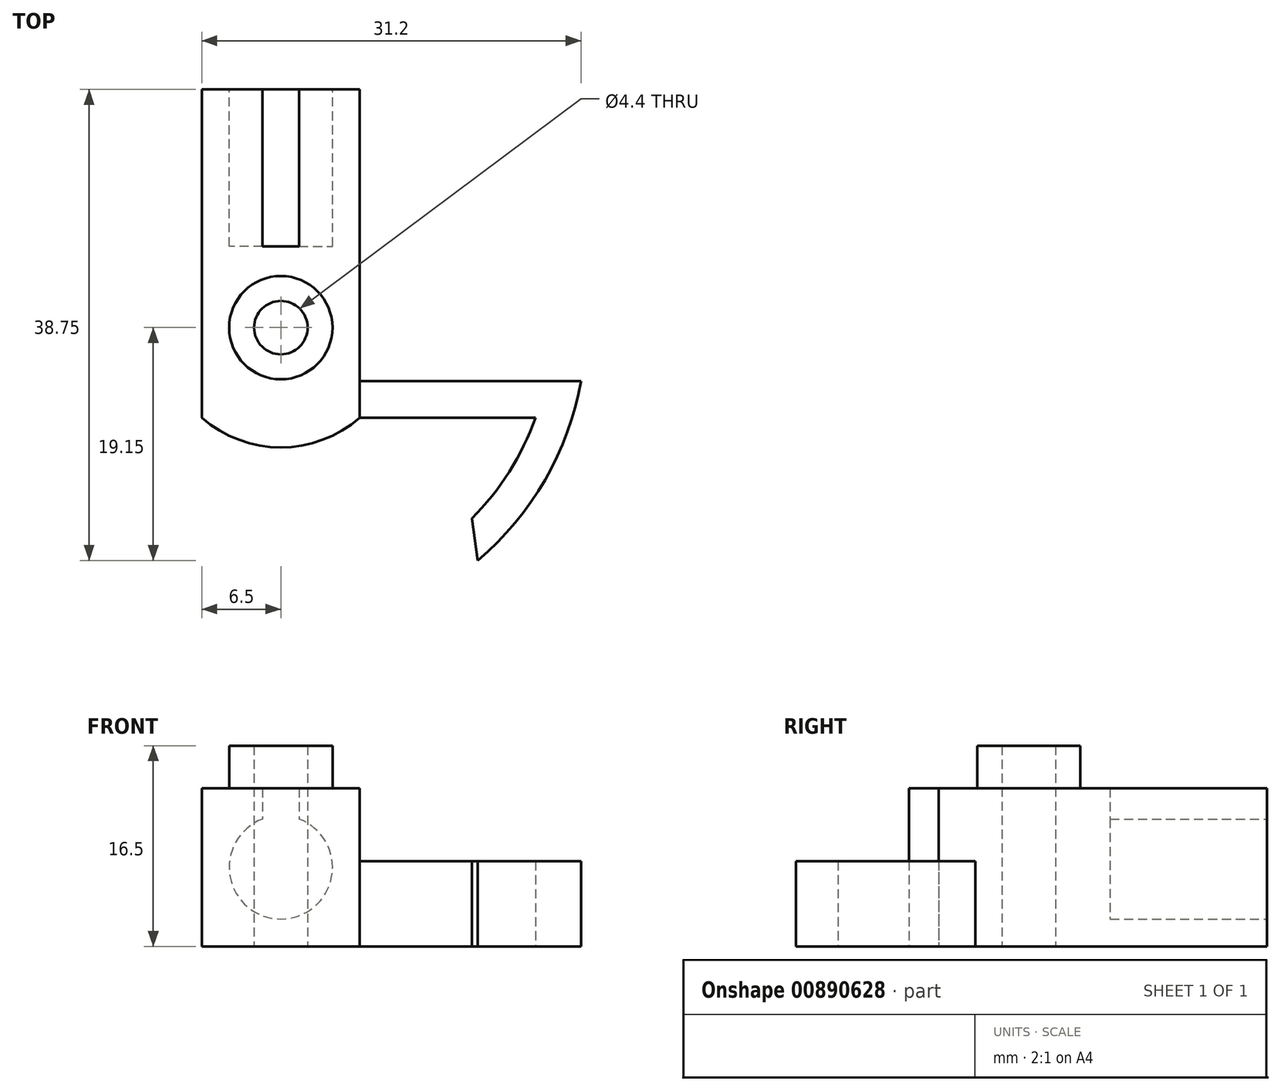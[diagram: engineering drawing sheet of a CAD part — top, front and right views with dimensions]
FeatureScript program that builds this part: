
annotation { "Feature Type Name" : "Feature", "Feature Type Description" : "" }
export const myFeature = defineFeature(function(context is Context, id is Id, definition is map)
    precondition{}
    {
        {
            var Q0;
            Q0=qCreatedBy(makeId("Top.planeOp"),FACE);
            var sketch = newSketch(context, id + "F0", { "sketchPlane" : qUnion([Q0])});
            skCircle(sketch, "E0", {"center": v(0, 0) * mm, "radius": 22.22 * mm, "construction": true});
            skLineSegment(sketch, "E1", {"start": v(0, 0) * mm, "end": v(-15.71, -15.71) * mm, "construction": true});
            skLineSegment(sketch, "E2", {"start": v(0, 0) * mm, "end": v(15.71, -15.71) * mm, "construction": true});
            skLineSegment(sketch, "E3", {"start": v(-6.5, -4.4) * mm, "end": v(6.5, -4.4) * mm});
            skLineSegment(sketch, "E4", {"start": v(-20.95, -7.4) * mm, "end": v(20.95, -7.4) * mm, "construction": true});
            skLineSegment(sketch, "E5", {"start": v(-15.71, -15.71) * mm, "end": v(15.71, -15.71) * mm, "construction": true});
            skArc(sketch, "E6", {"start": v(-11.71, -15.71) * mm, "mid": v(-15.5, -12) * mm, "end": v(-18.15, -7.4) * mm});
            skArc(sketch, "E7", {"start": v(15.71, -15.71) * mm, "mid": v(18.8, -11.85) * mm, "end": v(20.95, -7.4) * mm});
            skLineSegment(sketch, "E8", {"start": v(15.71, -15.71) * mm, "end": v(16.21, -19.15) * mm});
            skArc(sketch, "E9", {"start": v(16.21, -19.15) * mm, "mid": v(21.75, -12.52) * mm, "end": v(24.7, -4.4) * mm});
            skLineSegment(sketch, "E10", {"start": v(-18.15, -7.4) * mm, "end": v(20.95, -7.4) * mm});
            skLineSegment(sketch, "E11", {"start": v(-15.71, -15.71) * mm, "end": v(-11.71, -15.71) * mm});
            skLineSegment(sketch, "E12", {"start": v(20.95, -7.4) * mm, "end": v(23.95, -7.4) * mm, "construction": true});
            skLineSegment(sketch, "E13", {"start": v(-6.5, 19.6) * mm, "end": v(-6.5, -4.4) * mm});
            skLineSegment(sketch, "E14", {"start": v(-6.5, 19.6) * mm, "end": v(6.5, 19.6) * mm});
            skLineSegment(sketch, "E15", {"start": v(6.5, 19.6) * mm, "end": v(6.5, -4.4) * mm});
            skLineSegment(sketch, "E16", {"start": v(-6.5, -4.4) * mm, "end": v(-6.5, -7.4) * mm});
            skLineSegment(sketch, "E17", {"start": v(6.5, -4.4) * mm, "end": v(6.5, -7.4) * mm});
            skArc(sketch, "E18", {"start": v(-6.5, -7.4) * mm, "mid": v(0, -9.85) * mm, "end": v(6.5, -7.4) * mm});
            skLineSegment(sketch, "E19", {"start": v(6.5, -4.4) * mm, "end": v(24.7, -4.4) * mm});
            skLineSegment(sketch, "E20", {"start": v(-6.5, -4.4) * mm, "end": v(-21.78, -4.4) * mm});
            skArc(sketch, "E21", {"start": v(-21.78, -4.4) * mm, "mid": v(-19.58, -10.5) * mm, "end": v(-15.71, -15.71) * mm});
            skSolve(sketch);
        }
        {
            var Q0;
            Q0=qCreatedBy(makeId("Top.planeOp"),FACE);
            var sketch = newSketch(context, id + "F1", { "sketchPlane" : qUnion([Q0])});
            skCircle(sketch, "E22", {"center": v(0, 0) * mm, "radius": 2.2 * mm});
            skCircle(sketch, "E23", {"center": v(0, 0) * mm, "radius": 4.25 * mm});
            skSolve(sketch);
        }
        {
            var Q0;
            Q0=makeQuery(id+"F0.imprint","IMPRINT",FACE,{"disambiguationData":[TD([[makeQuery(id+"F0.imprint","IMPRINT",EDGE,{"derivedFrom":sQuery(id+"F0.wireOp",EDGE,"E3")}),1.0]])]});
            var Q1;
            Q1=makeQuery(id+"F0.imprint","IMPRINT",FACE,{"disambiguationData":[TD([[makeQuery(id+"F0.imprint","IMPRINT",EDGE,{"derivedFrom":sQuery(id+"F0.wireOp",EDGE,"E3")}),-1.0]])]});
            var Q2;
            {var subQ0=sQuery(id+"F0.wireOp",EDGE,"E18");Q2=makeQuery(id+"F0.imprint","IMPRINT",FACE,{"disambiguationData":[TD([[makeQuery(id+"F0.imprint","IMPRINT",EDGE,{"derivedFrom":subQ0}),1.0]])]});}
            extrude(context, id + "F2", {"entities" : qUnion([Q0, Q1, Q2]), "depth" : 13 * mm, "offsetDistance" : 25 * mm});
        }
        {
            var Q0;
            Q0=makeQuery(id+"F1.imprint","IMPRINT",FACE,{"disambiguationData":[TD([[makeQuery(id+"F1.imprint","IMPRINT",EDGE,{"derivedFrom":sQuery(id+"F1.wireOp",EDGE,"E22")}),1.0]])]});
            var Q1;
            Q1=makeQuery(id+"F2.opExtrude","CAP_FACE",FACE,{"disambiguationData":[OSD([sQuery(id+"F0.wireOp",EDGE,"E3"),sQuery(id+"F0.wireOp",EDGE,"KbbF9yi9-xrPk-JePT-w6c5-kPLa8MpGTuoP"),sQuery(id+"F0.wireOp",EDGE,"eadea0ab-e075-4038-b9cd-73dca94fccad"),sQuery(id+"F0.wireOp",EDGE,"E6"),sQuery(id+"F0.wireOp",EDGE,"E7"),sQuery(id+"F0.wireOp",EDGE,"E8"),sQuery(id+"F0.wireOp",EDGE,"E9"),sQuery(id+"F0.wireOp",EDGE,"E10"),sQuery(id+"F0.wireOp",EDGE,"hkPcLw81-8III-o7XO-lbjo-IzFt7Bc78l21"),sQuery(id+"F0.wireOp",EDGE,"Xk3sj3rP-0Nv0-YBO2-xSXg-Fs2LWpVnRU2r"),sQuery(id+"F0.wireOp",EDGE,"E11"),sQuery(id+"F0.wireOp",EDGE,"c4789ed1-a124-472e-85bf-6a12fd7359ae"),sQuery(id+"F0.wireOp",EDGE,"4b91fc80-4ab7-43a4-bafb-29e8abb85020"),sQuery(id+"F0.wireOp",EDGE,"E13"),sQuery(id+"F0.wireOp",EDGE,"E14"),sQuery(id+"F0.wireOp",EDGE,"E15"),sQuery(id+"F0.wireOp",EDGE,"E18")])],"isStart":false});
            extrude(context, id + "F3", {"entities" : qUnion([Q0]), "operationType" : NewBodyOperationType.REMOVE, "endBound" : BoundingType.UP_TO_SURFACE, "depth" : 25 * mm, "endBoundEntityFace" : qUnion([Q1]), "offsetDistance" : 25 * mm});
        }
        {
            var Q0;
            Q0=makeQuery(id+"F2.opExtrude","SWEPT_FACE",FACE,{"disambiguationData":[OSD([sQuery(id+"F0.wireOp",EDGE,"E14")])]});
            var sketch = newSketch(context, id + "F4", { "sketchPlane" : qUnion([Q0])});
            skLineSegment(sketch, "E24", {"start": v(-6.5, 6.5) * mm, "end": v(0, 6.5) * mm, "construction": true});
            skCircle(sketch, "E25", {"center": v(0, 6.5) * mm, "radius": 4.25 * mm});
            skLineSegment(sketch, "E26", {"start": v(-1.5, 13) * mm, "end": v(-1.5, 10.48) * mm});
            skLineSegment(sketch, "E27", {"start": v(1.5, 13) * mm, "end": v(1.5, 10.48) * mm});
            skSolve(sketch);
        }
        {
            var Q0;
            {var subQ0=sQuery(id+"F4.wireOp",EDGE,"E25");var subQ1=makeQuery(id+"F4.imprint","INTERSECT",VERTEX,{"derivedFrom":[subQ0,sQuery(id+"F4.wireOp",EDGE,"E26")]});Q0=makeQuery(id+"F4.imprint","IMPRINT",FACE,{"disambiguationData":[TD([[makeQuery(id+"F4.imprint","IMPRINT",EDGE,{"disambiguationData":[TD([[subQ1,1.0]])],"derivedFrom":subQ0}),1.0]])]});}
            var Q1;
            {var subQ0=sQuery(id+"F4.wireOp",EDGE,"E26");Q1=makeQuery(id+"F4.imprint","IMPRINT",FACE,{"disambiguationData":[TD([[makeQuery(id+"F4.imprint","IMPRINT",EDGE,{"derivedFrom":subQ0}),1.0]])]});}
            extrude(context, id + "F5", {"entities" : qUnion([Q0, Q1]), "operationType" : NewBodyOperationType.REMOVE, "oppositeDirection" : true, "depth" : 12.9 * mm, "offsetDistance" : 25 * mm});
        }
        {
            var Q0;
            {var subQ1=sQuery(id+"F0.wireOp",EDGE,"E7");Q0=makeQuery(id+"F0.imprint","IMPRINT",FACE,{"disambiguationData":[TD([[makeQuery(id+"F0.imprint","IMPRINT",EDGE,{"derivedFrom":subQ1}),-1.0]])]});}
            var Q1;
            {var subQ1=sQuery(id+"F0.wireOp",EDGE,"E6");Q1=makeQuery(id+"F0.imprint","IMPRINT",FACE,{"disambiguationData":[TD([[makeQuery(id+"F0.imprint","IMPRINT",EDGE,{"derivedFrom":subQ1}),1.0]])]});}
            extrude(context, id + "F6", {"entities" : qUnion([Q0, Q1]), "operationType" : NewBodyOperationType.ADD, "depth" : 7 * mm, "offsetDistance" : 25 * mm});
        }
        {
            var Q0;
            Q0 = qSketchRegion(id + "F1", true);
            extrude(context, id + "F7", {"entities" : qUnion([Q0]), "operationType" : NewBodyOperationType.ADD, "depth" : 16.5 * mm, "offsetDistance" : 25 * mm});
        }
    });
